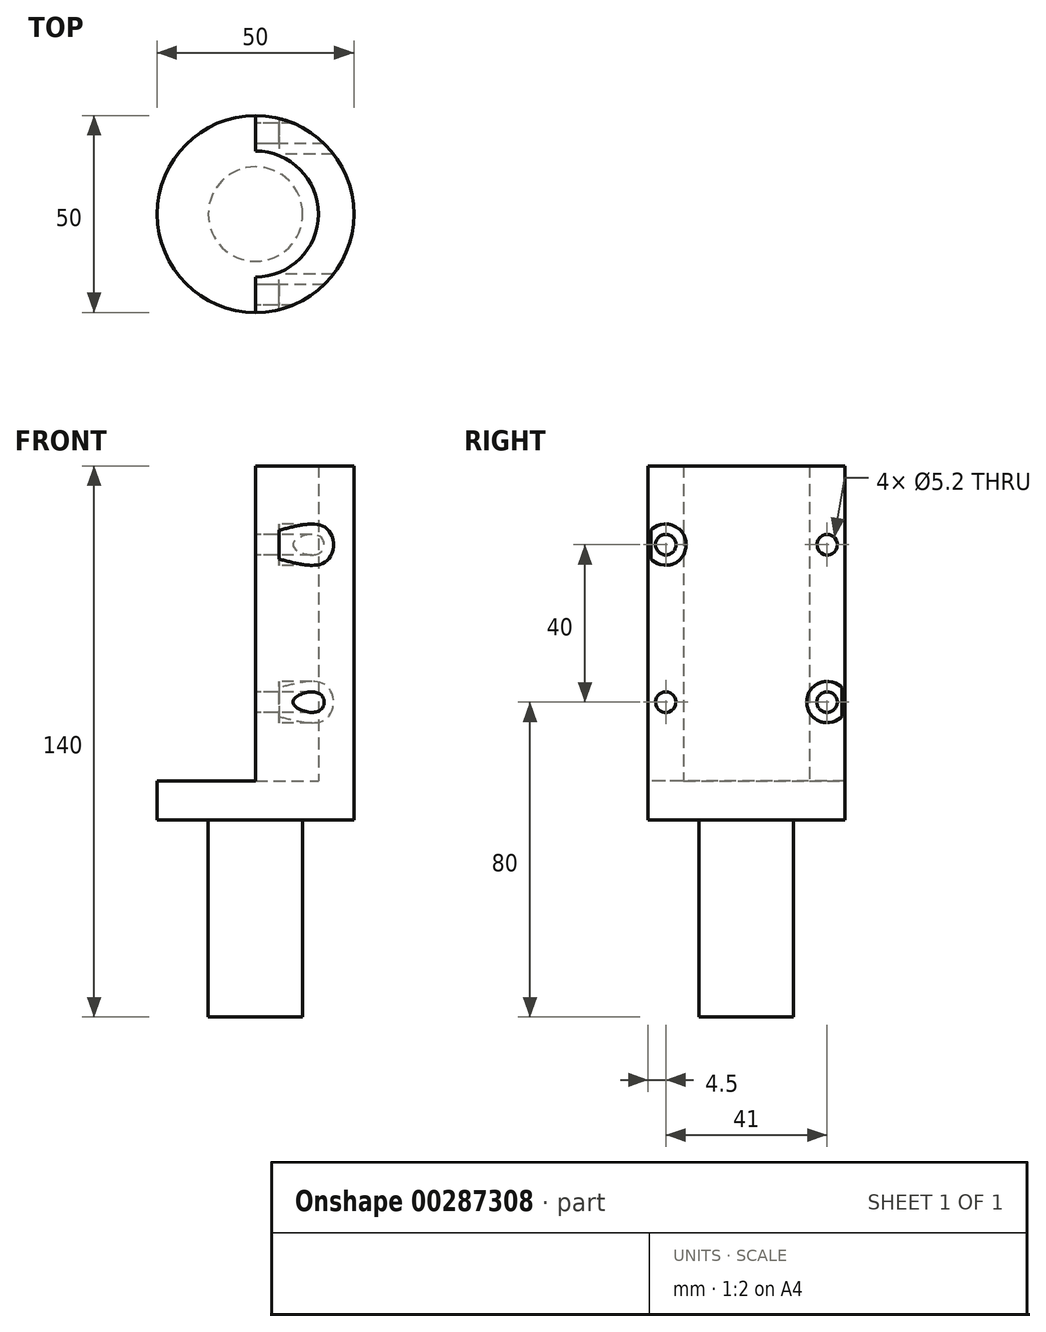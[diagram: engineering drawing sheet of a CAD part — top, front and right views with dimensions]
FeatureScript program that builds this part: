
annotation { "Feature Type Name" : "Feature", "Feature Type Description" : "" }
export const myFeature = defineFeature(function(context is Context, id is Id, definition is map)
    precondition{}
    {
        {
            var Q0;
            Q0=qCreatedBy(makeId("Top.planeOp"),FACE);
            var sketch = newSketch(context, id + "F0", { "sketchPlane" : qUnion([Q0])});
            skCircle(sketch, "E0", {"center": v(0, 0) * mm, "radius": 12 * mm});
            skSolve(sketch);
        }
        {
            var Q0;
            Q0 = qSketchRegion(id + "F0", true);
            extrude(context, id + "F1", {"entities" : qUnion([Q0]), "depth" : 50 * mm});
        }
        {
            var Q0;
            Q0=makeQuery(id+"F1.opExtrude","CAP_FACE",FACE,{"disambiguationData":[OSD([sQuery(id+"F0.wireOp",EDGE,"E0")])],"isStart":false});
            var sketch = newSketch(context, id + "F2", { "sketchPlane" : qUnion([Q0])});
            skCircle(sketch, "E1", {"center": v(0, 0) * mm, "radius": 25 * mm});
            skSolve(sketch);
        }
        {
            var Q0;
            Q0 = qSketchRegion(id + "F2", true);
            extrude(context, id + "F3", {"entities" : qUnion([Q0]), "operationType" : NewBodyOperationType.ADD, "depth" : 10 * mm});
        }
        {
            var Q0;
            Q0=makeQuery(id+"F3.opExtrude","CAP_FACE",FACE,{"disambiguationData":[OSD([sQuery(id+"F2.wireOp",EDGE,"E1")])],"isStart":false});
            var sketch = newSketch(context, id + "F4", { "sketchPlane" : qUnion([Q0])});
            skArc(sketch, "E2", {"start": v(0, -16) * mm, "mid": v(16, 0) * mm, "end": v(0, 16) * mm});
            skArc(sketch, "E3", {"start": v(0, -25) * mm, "mid": v(25, 0) * mm, "end": v(0, 25) * mm});
            skLineSegment(sketch, "E4", {"start": v(0, 16) * mm, "end": v(0, 25) * mm});
            skLineSegment(sketch, "E5", {"start": v(0, -16) * mm, "end": v(0, -25) * mm});
            skSolve(sketch);
        }
        {
            var Q0;
            Q0=makeQuery(id+"F4.imprint","IMPRINT",FACE,{"disambiguationData":[TD([[makeQuery(id+"F4.imprint","IMPRINT",EDGE,{"derivedFrom":sQuery(id+"F4.wireOp",EDGE,"E2")}),-1.0]])]});
            extrude(context, id + "F5", {"entities" : qUnion([Q0]), "operationType" : NewBodyOperationType.ADD, "depth" : 80 * mm});
        }
        {
            var Q0;
            Q0=makeQuery(id+"F5.opExtrude","SWEPT_FACE",FACE,{"disambiguationData":[OSD([sQuery(id+"F4.wireOp",EDGE,"E5")])]});
            var sketch = newSketch(context, id + "F6", { "sketchPlane" : qUnion([Q0])});
            skCircle(sketch, "E6", {"center": v(20.5, 80) * mm, "radius": 2.6 * mm});
            skPoint(sketch, "E6.centerSnap0", {"position": v(20.5, 60) * mm});
            skCircle(sketch, "E7", {"center": v(20.5, 120) * mm, "radius": 2.6 * mm});
            skCircle(sketch, "E8", {"center": v(-20.5, 120) * mm, "radius": 2.6 * mm});
            skCircle(sketch, "E9", {"center": v(-20.5, 80) * mm, "radius": 2.6 * mm});
            skSolve(sketch);
        }
        {
            var Q0;
            Q0 = qSketchRegion(id + "F6", true);
            extrude(context, id + "F7", {"entities" : qUnion([Q0]), "operationType" : NewBodyOperationType.REMOVE, "endBound" : BoundingType.THROUGH_ALL, "oppositeDirection" : true, "depth" : 25 * mm});
        }
        {
            var Q0;
            Q0=makeQuery(id+"F5.opExtrude","SWEPT_FACE",FACE,{"disambiguationData":[OSD([sQuery(id+"F4.wireOp",EDGE,"E5")])]});
            cPlane(context, id + "F8", {"entities" : qUnion([Q0]), "cplaneType" : CPlaneType.OFFSET, "offset" : 6 * mm, "oppositeDirection" : true, "width" : 150 * mm, "height" : 150 * mm});
        }
        {
            var Q0;
            Q0=qCreatedBy(id+"F8.planeOp",FACE);
            var sketch = newSketch(context, id + "F9", { "sketchPlane" : qUnion([Q0])});
            skCircle(sketch, "E10", {"center": v(20.5, 120) * mm, "radius": 5.25 * mm});
            skLineSegment(sketch, "E11", {"start": v(20.5, 120) * mm, "end": v(20.5, 80) * mm});
            skLineSegment(sketch, "E12", {"start": v(20.5, 80) * mm, "end": v(-20.5, 80) * mm});
            skCircle(sketch, "E13", {"center": v(-20.5, 80) * mm, "radius": 5.25 * mm});
            skSolve(sketch);
        }
        {
            var Q0;
            Q0 = qSketchRegion(id + "F9", true);
            extrude(context, id + "F10", {"entities" : qUnion([Q0]), "operationType" : NewBodyOperationType.REMOVE, "oppositeDirection" : true, "depth" : 25 * mm});
        }
    });
